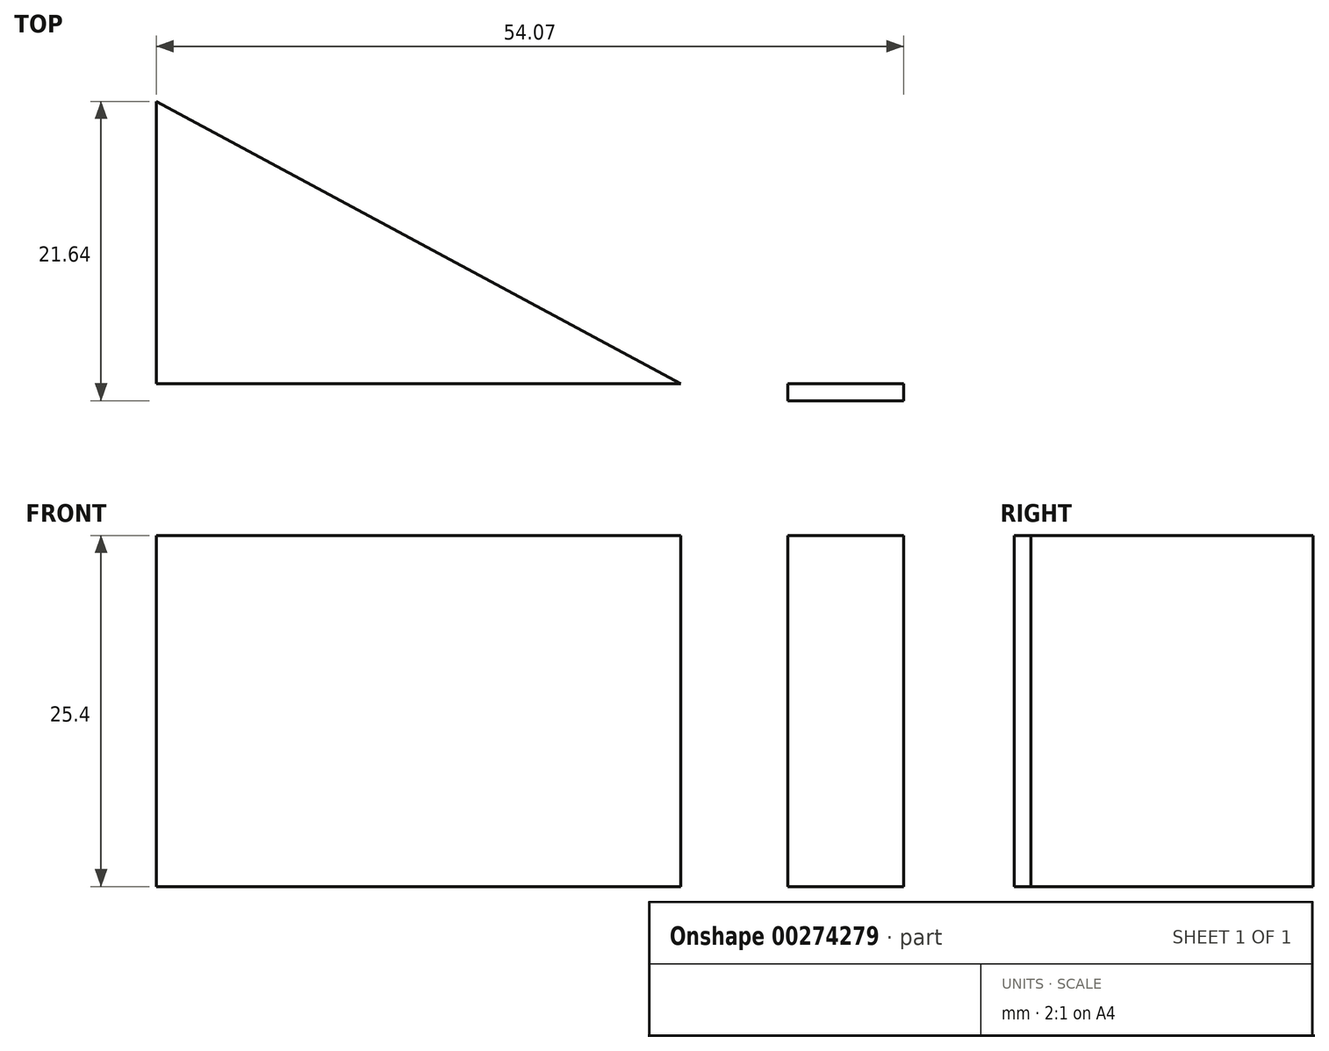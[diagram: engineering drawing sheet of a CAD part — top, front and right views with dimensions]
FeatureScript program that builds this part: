
annotation { "Feature Type Name" : "Feature", "Feature Type Description" : "" }
export const myFeature = defineFeature(function(context is Context, id is Id, definition is map)
    precondition{}
    {
        {
            var Q0;
            Q0=qCreatedBy(makeId("Top.planeOp"),FACE);
            var sketch = newSketch(context, id + "F0", { "sketchPlane" : qUnion([Q0])});
            skLineSegment(sketch, "E0.bottom", {"start": v(0, 0) * mm, "end": v(-54.07, 0) * mm});
            skLineSegment(sketch, "E0.top", {"start": v(0, 0) * mm, "end": v(-54.07, 0) * mm});
            skLineSegment(sketch, "E0.left", {"start": v(0, 0) * mm, "end": v(0, 0) * mm});
            skLineSegment(sketch, "E0.right", {"start": v(-54.07, 0) * mm, "end": v(-54.07, 0) * mm});
            skLineSegment(sketch, "E1.bottom", {"start": v(-8.4, -1.2) * mm, "end": v(0, -1.2) * mm});
            skLineSegment(sketch, "E1.top", {"start": v(-8.4, 0) * mm, "end": v(0, 0) * mm});
            skLineSegment(sketch, "E1.left", {"start": v(-8.4, -1.2) * mm, "end": v(-8.4, 0) * mm});
            skLineSegment(sketch, "E1.right", {"start": v(0, -1.2) * mm, "end": v(0, 0) * mm});
            skLineSegment(sketch, "E2", {"start": v(-54.07, 0) * mm, "end": v(-54.07, 61.74) * mm});
            skLineSegment(sketch, "E3", {"start": v(-54.6, 63.54) * mm, "end": v(0, 61.74) * mm});
            skLineSegment(sketch, "E4", {"start": v(0, 61.74) * mm, "end": v(-2.66, 64.44) * mm});
            skLineSegment(sketch, "E5", {"start": v(0, 61.74) * mm, "end": v(0, -1.2) * mm});
            skLineSegment(sketch, "E6", {"start": v(31.78, -25.8) * mm, "end": v(-186.08, 91.52) * mm});
            skSolve(sketch);
        }
        {
            var Q0;
            Q0 = qSketchRegion(id + "F0", true);
            extrude(context, id + "F1", {"entities" : qUnion([Q0]), "depth" : 25.4 * mm});
        }
    });
